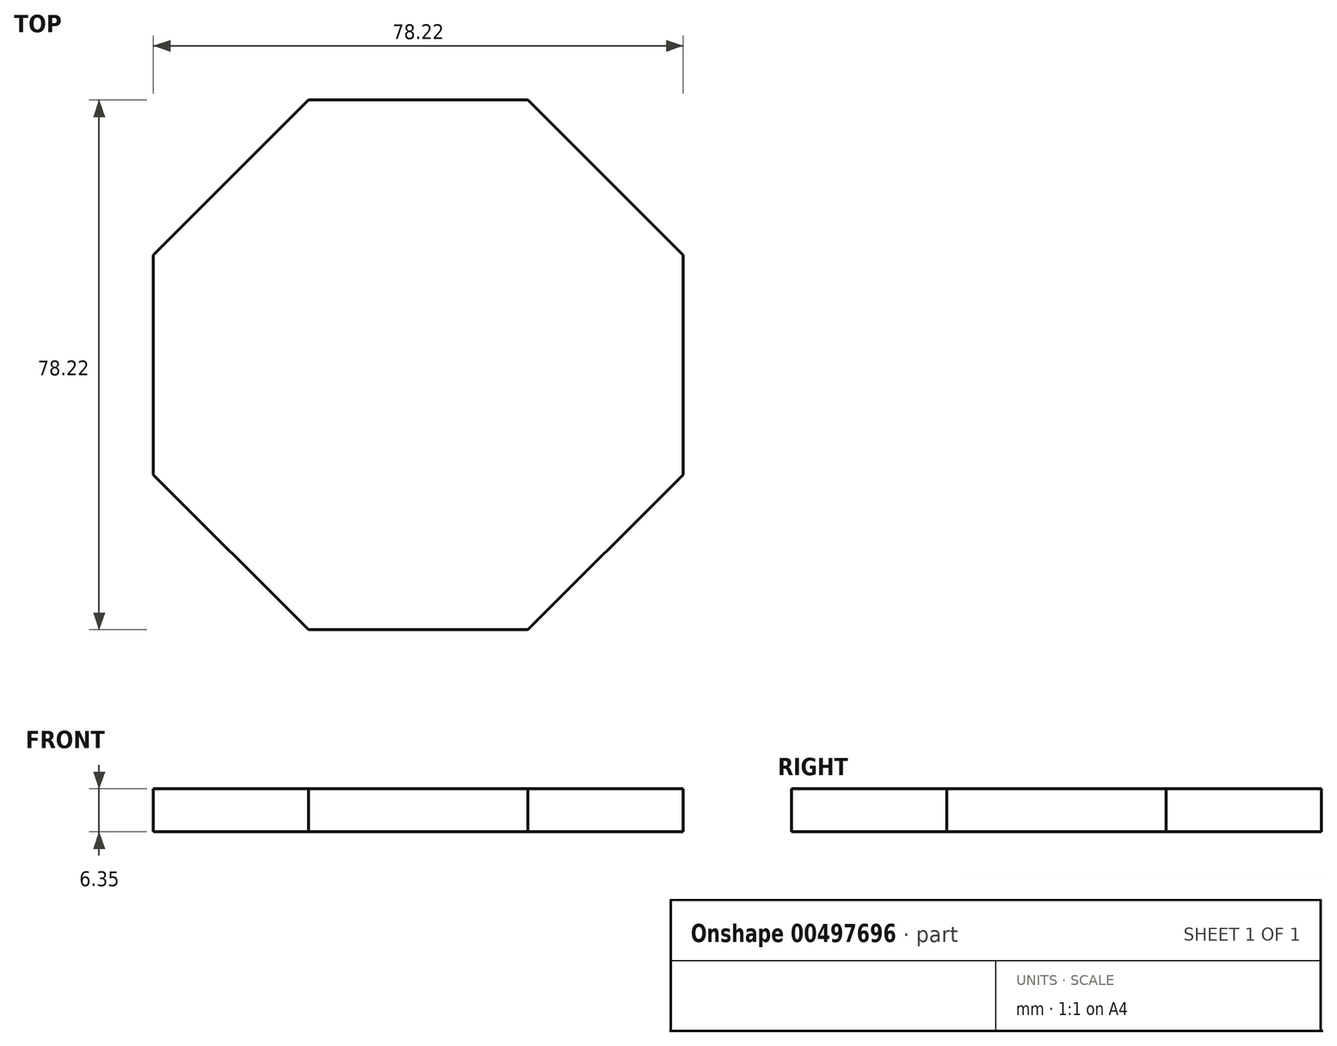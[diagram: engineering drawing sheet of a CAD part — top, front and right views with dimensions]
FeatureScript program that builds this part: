
annotation { "Feature Type Name" : "Feature", "Feature Type Description" : "" }
export const myFeature = defineFeature(function(context is Context, id is Id, definition is map)
    precondition{}
    {
        {
            var Q0;
            Q0=qCreatedBy(makeId("Top.planeOp"),FACE);
            var sketch = newSketch(context, id + "F0", { "sketchPlane" : qUnion([Q0])});
            skCircle(sketch, "E0.cCircle", {"center": v(0, 0) * mm, "radius": 42.34 * mm, "construction": true});
            skLineSegment(sketch, "E0.0", {"start": v(39.11, 16.2) * mm, "end": v(39.11, -16.2) * mm});
            skLineSegment(sketch, "E0.1", {"start": v(39.11, -16.2) * mm, "end": v(16.2, -39.11) * mm});
            skLineSegment(sketch, "E0.2", {"start": v(16.2, -39.11) * mm, "end": v(-16.2, -39.11) * mm});
            skLineSegment(sketch, "E0.3", {"start": v(-16.2, -39.11) * mm, "end": v(-39.11, -16.2) * mm});
            skLineSegment(sketch, "E0.4", {"start": v(-39.11, -16.2) * mm, "end": v(-39.11, 16.2) * mm});
            skLineSegment(sketch, "E0.5", {"start": v(-39.11, 16.2) * mm, "end": v(-16.2, 39.11) * mm});
            skLineSegment(sketch, "E0.6", {"start": v(-16.2, 39.11) * mm, "end": v(16.2, 39.11) * mm});
            skLineSegment(sketch, "E0.7", {"start": v(16.2, 39.11) * mm, "end": v(39.11, 16.2) * mm});
            skSolve(sketch);
        }
        {
            var Q0;
            Q0=makeQuery(id+"F0.imprint","IMPRINT",FACE,{"disambiguationData":[TD([[makeQuery(id+"F0.imprint","IMPRINT",EDGE,{"derivedFrom":sQuery(id+"F0.wireOp",EDGE,"E0.0")}),-1.0]])]});
            extrude(context, id + "F1", {"entities" : qUnion([Q0]), "depth" : 6.35 * mm});
        }
    });
